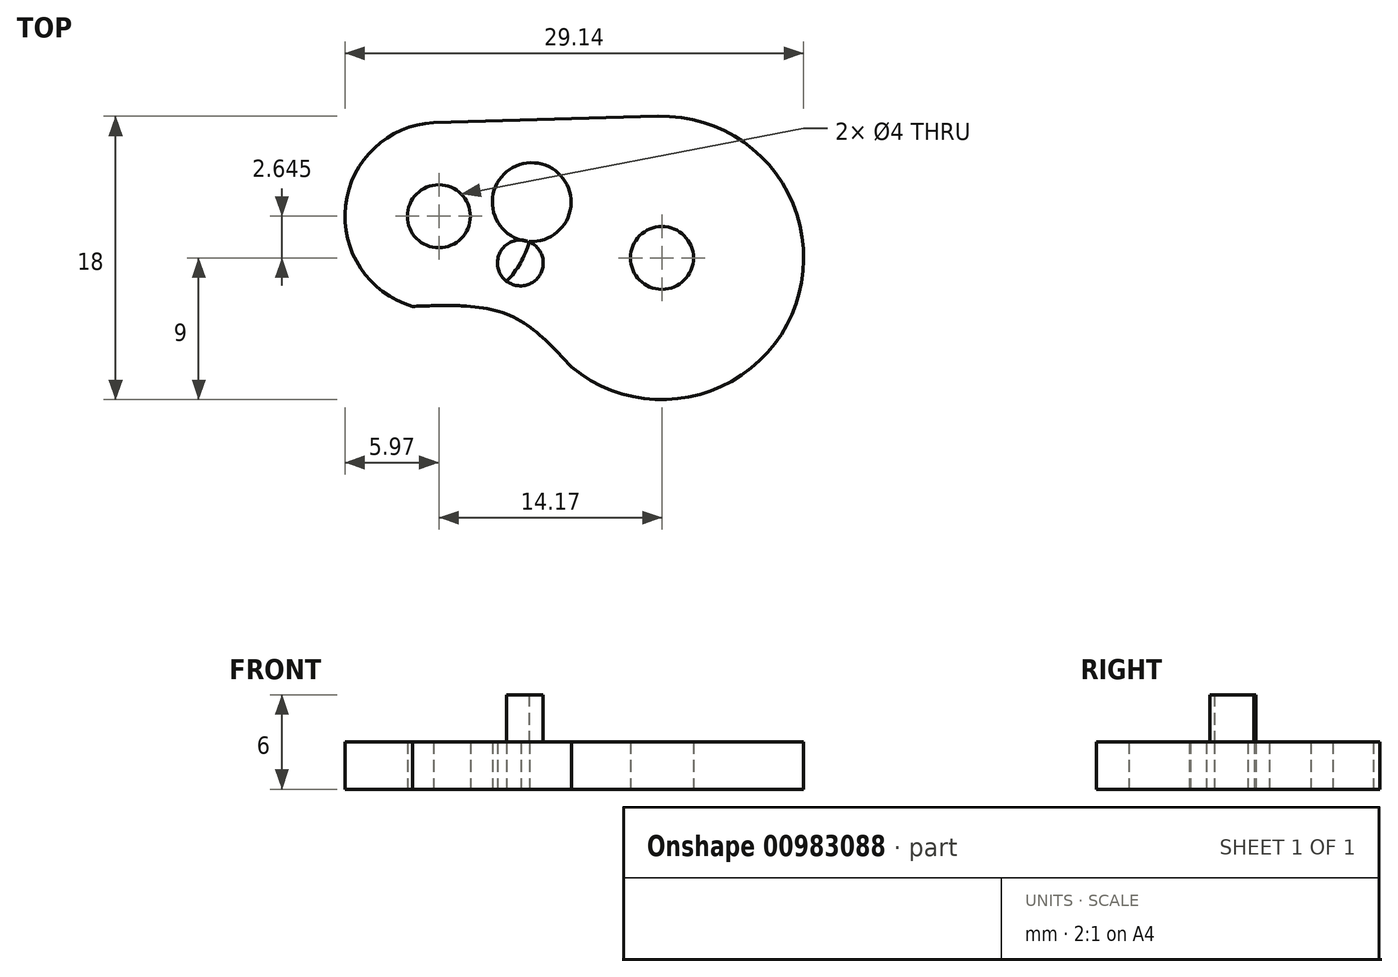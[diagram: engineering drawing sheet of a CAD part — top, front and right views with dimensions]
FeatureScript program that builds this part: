
annotation { "Feature Type Name" : "Feature", "Feature Type Description" : "" }
export const myFeature = defineFeature(function(context is Context, id is Id, definition is map)
    precondition{}
    {
        {
            var Q0;
            Q0=qCreatedBy(makeId("Top.planeOp"),FACE);
            var sketch = newSketch(context, id + "F0", { "sketchPlane" : qUnion([Q0])});
            skCircle(sketch, "E0", {"center": v(0, 0) * mm, "radius": 9 * mm});
            skCircle(sketch, "E1", {"center": v(0, 0) * mm, "radius": 2 * mm});
            skCircle(sketch, "E2", {"center": v(-14.17, 2.65) * mm, "radius": 2 * mm});
            skLineSegment(sketch, "E3", {"start": v(-15, 8.59) * mm, "end": v(0, 9) * mm});
            skCircle(sketch, "E4", {"center": v(-14.17, 2.65) * mm, "radius": 5.97 * mm});
            skFitSpline(sketch, "E5", {"points": [v(-15.85, -3.08) * mm, v(-9.78, -3.6) * mm, v(-5.74, -6.94) * mm], "startDerivative": vector(12.55, 0.5) * mm, "endDerivative": vector(7.61, -8.33) * mm});
            skCircle(sketch, "E6", {"center": v(-9, -0.32) * mm, "radius": 1.45 * mm});
            skCircle(sketch, "E7", {"center": v(-8.27, 3.54) * mm, "radius": 2.5 * mm});
            skSolve(sketch);
        }
        {
            var Q0;
            Q0=makeQuery(id+"F0.imprint","IMPRINT",FACE,{"disambiguationData":[TD([[makeQuery(id+"F0.imprint","IMPRINT",EDGE,{"derivedFrom":sQuery(id+"F0.wireOp",EDGE,"RhsbrpbH-C4ei-NZDm-gsTT-VSSDbBvhbBTT")}),1.0]])]});
            var Q1;
            Q1=makeQuery(id+"F0.imprint","IMPRINT",FACE,{"disambiguationData":[TD([[makeQuery(id+"F0.imprint","IMPRINT",EDGE,{"derivedFrom":sQuery(id+"F0.wireOp",EDGE,"RhsbrpbH-C4ei-NZDm-gsTT-VSSDbBvhbBTT")}),-1.0]])]});
            var Q2;
            Q2=makeQuery(id+"F0.imprint","IMPRINT",FACE,{"disambiguationData":[TD([[makeQuery(id+"F0.imprint","IMPRINT",EDGE,{"derivedFrom":sQuery(id+"F0.wireOp",EDGE,"E1")}),-1.0]])]});
            var Q3;
            {var subQ0=sQuery(id+"F0.wireOp",EDGE,"E5");var subQ1=sQuery(id+"F0.wireOp",EDGE,"E0");var subQ2=makeQuery(id+"F0.imprint","INTERSECT",VERTEX,{"disambiguationData":[OD(1.0)],"derivedFrom":[subQ1,subQ0]});Q3=makeQuery(id+"F0.imprint","IMPRINT",FACE,{"disambiguationData":[TD([[makeQuery(id+"F0.imprint","IMPRINT",EDGE,{"disambiguationData":[TD([[subQ2,1.0]])],"derivedFrom":subQ1}),-1.0]])]});}
            var Q4;
            {var subQ0=sQuery(id+"F0.wireOp",EDGE,"E3");var subQ1=sQuery(id+"F0.wireOp",EDGE,"E0");var subQ2=makeQuery(id+"F0.imprint","INTERSECT",VERTEX,{"derivedFrom":[subQ1,subQ0]});Q4=makeQuery(id+"F0.imprint","IMPRINT",FACE,{"disambiguationData":[TD([[makeQuery(id+"F0.imprint","IMPRINT",EDGE,{"disambiguationData":[TD([[subQ2,-1.0]])],"derivedFrom":subQ1}),-1.0]])]});}
            var Q5;
            Q5=makeQuery(id+"F0.imprint","IMPRINT",FACE,{"disambiguationData":[TD([[makeQuery(id+"F0.imprint","IMPRINT",EDGE,{"derivedFrom":sQuery(id+"F0.wireOp",EDGE,"E2")}),-1.0]])]});
            var Q6;
            Q6=makeQuery(id+"F0.imprint","IMPRINT",FACE,{"disambiguationData":[TD([[makeQuery(id+"F0.imprint","IMPRINT",EDGE,{"derivedFrom":sQuery(id+"F0.wireOp",EDGE,"E6")}),1.0]])]});
            extrude(context, id + "F1", {"entities" : qUnion([Q0, Q1, Q2, Q3, Q4, Q5, Q6]), "depth" : 3 * mm, "offsetDistance" : 25 * mm});
        }
        {
            var Q0;
            Q0=makeQuery(id+"F0.imprint","IMPRINT",FACE,{"disambiguationData":[TD([[makeQuery(id+"F0.imprint","IMPRINT",EDGE,{"derivedFrom":sQuery(id+"F0.wireOp",EDGE,"E6")}),1.0]])]});
            extrude(context, id + "F2", {"entities" : qUnion([Q0]), "operationType" : NewBodyOperationType.ADD, "depth" : 6 * mm, "offsetDistance" : 25 * mm});
        }
    });
